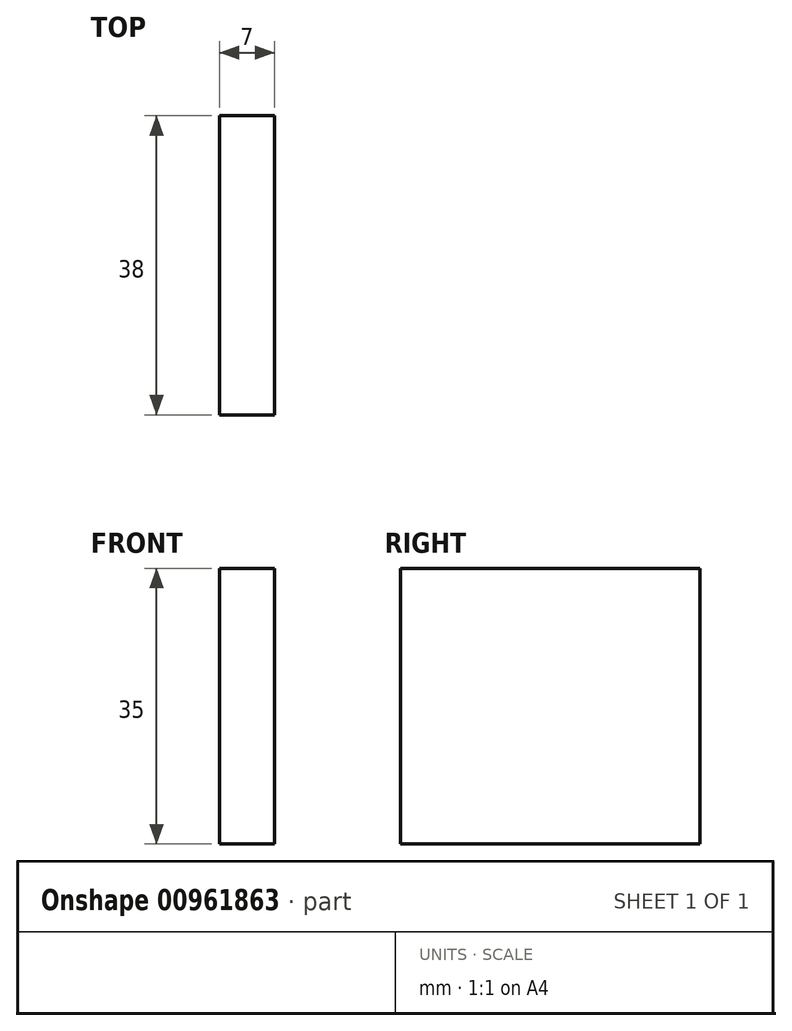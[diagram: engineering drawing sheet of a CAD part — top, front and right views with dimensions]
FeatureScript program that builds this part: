
annotation { "Feature Type Name" : "Feature", "Feature Type Description" : "" }
export const myFeature = defineFeature(function(context is Context, id is Id, definition is map)
    precondition{}
    {
        {
            var Q0;
            Q0=qCreatedBy(makeId("Top.planeOp"),FACE);
            var sketch = newSketch(context, id + "F0", { "sketchPlane" : qUnion([Q0])});
            skLineSegment(sketch, "E0.bottom", {"start": v(-35.6, 25.1) * mm, "end": v(-28.6, 25.1) * mm});
            skLineSegment(sketch, "E0.top", {"start": v(-35.6, -12.9) * mm, "end": v(-28.6, -12.9) * mm});
            skLineSegment(sketch, "E0.left", {"start": v(-35.6, 25.1) * mm, "end": v(-35.6, -12.9) * mm});
            skLineSegment(sketch, "E0.right", {"start": v(-28.6, 25.1) * mm, "end": v(-28.6, -12.9) * mm});
            skSolve(sketch);
        }
        {
            var Q0;
            Q0 = qSketchRegion(id + "F0", true);
            extrude(context, id + "F1", {"entities" : qUnion([Q0]), "depth" : 35 * mm, "offsetDistance" : 25 * mm});
        }
    });
